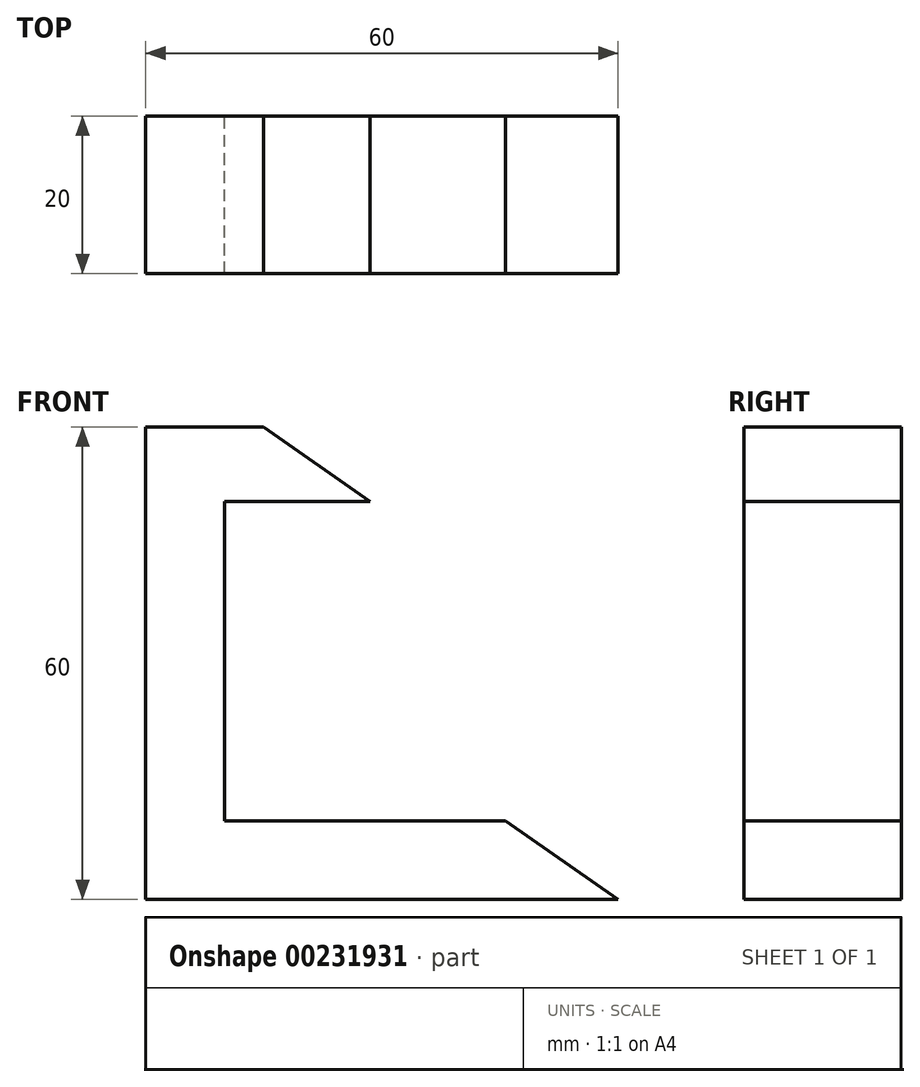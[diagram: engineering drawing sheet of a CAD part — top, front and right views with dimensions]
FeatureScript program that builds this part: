
annotation { "Feature Type Name" : "Feature", "Feature Type Description" : "" }
export const myFeature = defineFeature(function(context is Context, id is Id, definition is map)
    precondition{}
    {
        {
            var Q0;
            Q0=qCreatedBy(makeId("Front.planeOp"),FACE);
            var sketch = newSketch(context, id + "F0", { "sketchPlane" : qUnion([Q0])});
            skLineSegment(sketch, "E0", {"start": v(-45.94, 40.9) * mm, "end": v(-45.94, -19.1) * mm});
            skLineSegment(sketch, "E1", {"start": v(-45.94, -19.1) * mm, "end": v(14.06, -19.1) * mm});
            skLineSegment(sketch, "E2", {"start": v(14.06, -19.1) * mm, "end": v(-0.22, -9.1) * mm});
            skLineSegment(sketch, "E3", {"start": v(-0.22, -9.1) * mm, "end": v(-35.94, -9.1) * mm});
            skLineSegment(sketch, "E4", {"start": v(-35.94, -9.1) * mm, "end": v(-35.94, 31.45) * mm});
            skLineSegment(sketch, "E5", {"start": v(-35.94, 31.45) * mm, "end": v(-17.45, 31.45) * mm});
            skLineSegment(sketch, "E6", {"start": v(-17.45, 31.45) * mm, "end": v(-30.94, 40.9) * mm});
            skLineSegment(sketch, "E7", {"start": v(-30.94, 40.9) * mm, "end": v(-45.94, 40.9) * mm});
            skSolve(sketch);
        }
        {
            var Q0;
            Q0=makeQuery(id+"F0.imprint","IMPRINT",FACE,{"disambiguationData":[TD([[makeQuery(id+"F0.imprint","IMPRINT",EDGE,{"derivedFrom":sQuery(id+"F0.wireOp",EDGE,"E0")}),1.0]])]});
            extrude(context, id + "F1", {"entities" : qUnion([Q0]), "depth" : 20 * mm});
        }
    });
